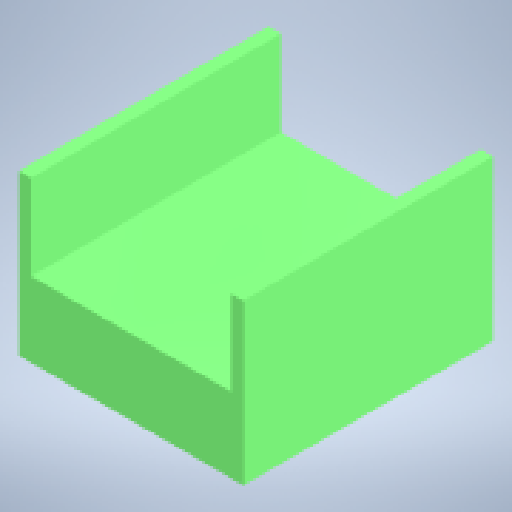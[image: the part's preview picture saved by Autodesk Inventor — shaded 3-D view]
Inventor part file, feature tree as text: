
AUTODESK INVENTOR PART (.ipt)
format: ipt  version: 2024 (Build 280153000, 153)  size: 138,240 bytes
history: native  units: mm
features: extrude x1, sketch x1
ambient origin geometry x8: Origin, YZ Plane, XZ Plane, XY Plane, X Axis, Y Axis, Z Axis, Center Point
bodies: Solido1 (feature_tree)
feature tree (2):
  extrude  "Estrusione1"  Depth=45.0mm
  sketch  "Schizzo1"
